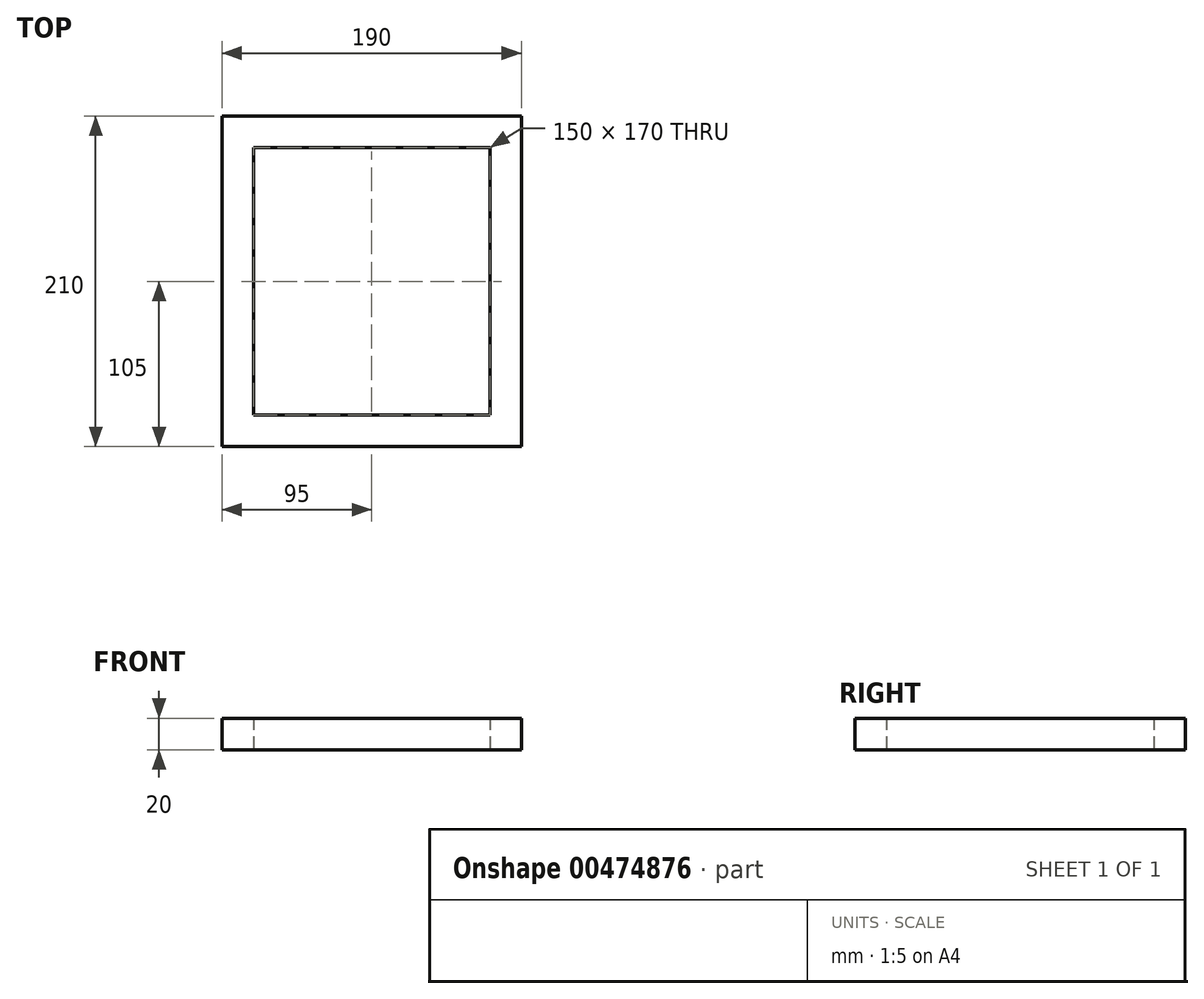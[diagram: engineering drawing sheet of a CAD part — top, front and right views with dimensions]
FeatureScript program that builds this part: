
annotation { "Feature Type Name" : "Feature", "Feature Type Description" : "" }
export const myFeature = defineFeature(function(context is Context, id is Id, definition is map)
    precondition{}
    {
        {
            var Q0;
            Q0=qCreatedBy(makeId("Top.planeOp"),FACE);
            var sketch = newSketch(context, id + "F0", { "sketchPlane" : qUnion([Q0])});
            skLineSegment(sketch, "E0.bottom", {"start": v(95, -105) * mm, "end": v(-95, -105) * mm});
            skLineSegment(sketch, "E0.top", {"start": v(95, 105) * mm, "end": v(-95, 105) * mm});
            skLineSegment(sketch, "E0.left", {"start": v(95, -105) * mm, "end": v(95, 105) * mm});
            skLineSegment(sketch, "E0.right", {"start": v(-95, -105) * mm, "end": v(-95, 105) * mm});
            skPoint(sketch, "E0.middle", {"position": v(0, 0) * mm});
            skLineSegment(sketch, "E1.bottom", {"start": v(75, -85) * mm, "end": v(-75, -85) * mm});
            skLineSegment(sketch, "E1.top", {"start": v(75, 85) * mm, "end": v(-75, 85) * mm});
            skLineSegment(sketch, "E1.left", {"start": v(75, -85) * mm, "end": v(75, 85) * mm});
            skLineSegment(sketch, "E1.right", {"start": v(-75, -85) * mm, "end": v(-75, 85) * mm});
            skSolve(sketch);
        }
        {
            var Q0;
            Q0 = qSketchRegion(id + "F0", true);
            extrude(context, id + "F1", {"entities" : qUnion([Q0]), "endBound" : BoundingType.SYMMETRIC, "depth" : 20 * mm});
        }
    });
